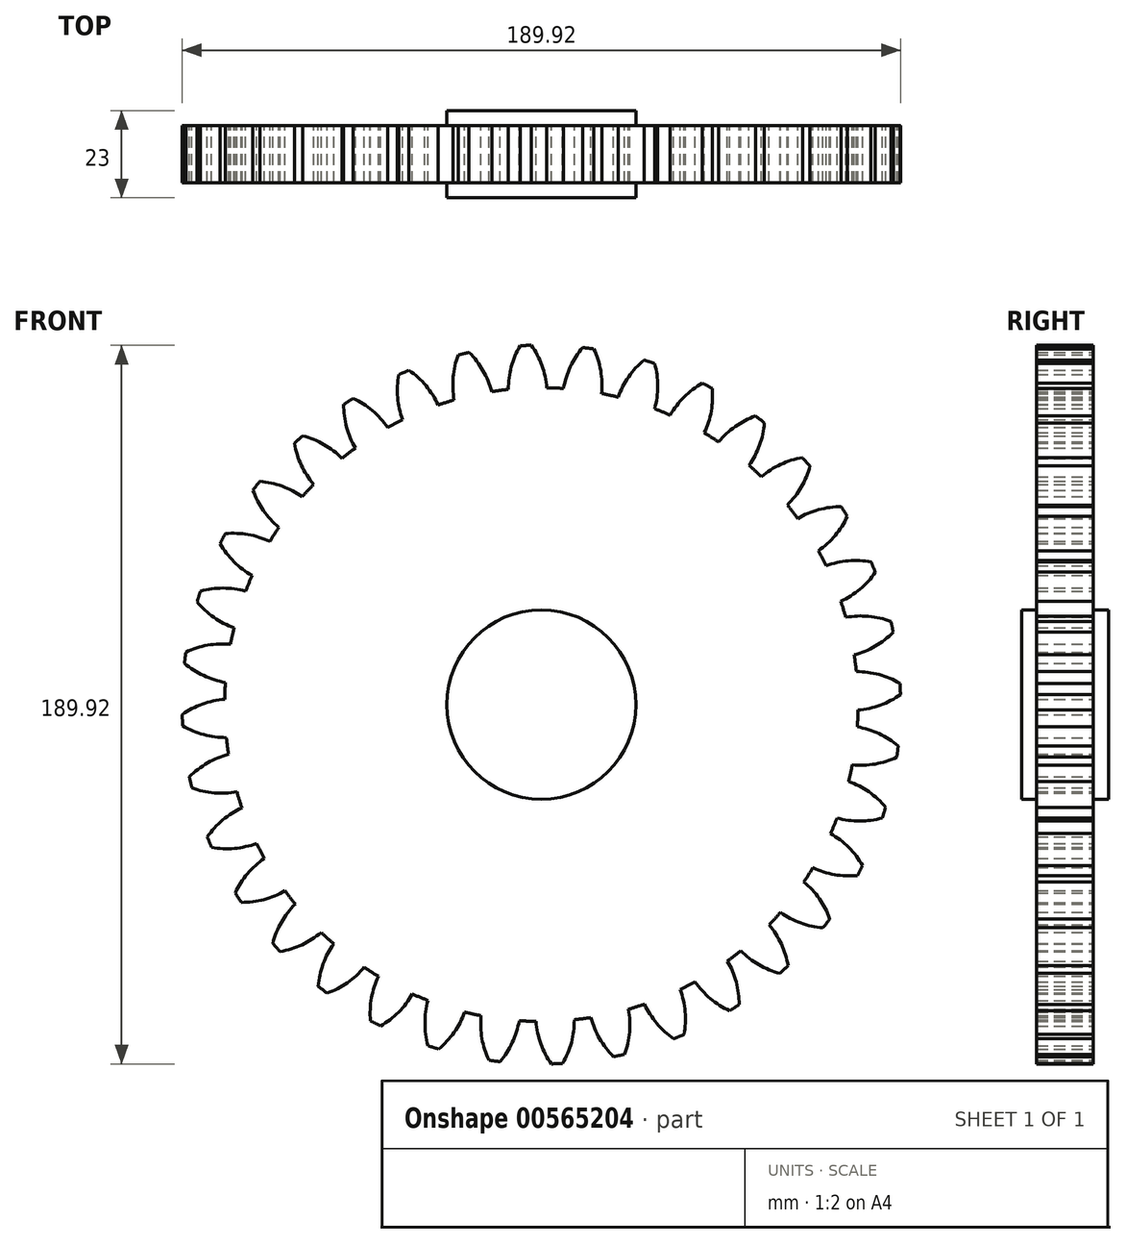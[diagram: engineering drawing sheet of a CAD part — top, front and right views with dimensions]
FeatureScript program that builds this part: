
annotation { "Feature Type Name" : "Feature", "Feature Type Description" : "" }
export const myFeature = defineFeature(function(context is Context, id is Id, definition is map)
    precondition{}
    {
        {
            var Q0;
            Q0=qCreatedBy(makeId("Front.planeOp"),FACE);
            var sketch = newSketch(context, id + "F0", { "sketchPlane" : qUnion([Q0])});
            skCircle(sketch, "E0", {"center": v(0, 0) * mm, "radius": 83.75 * mm});
            skCircle(sketch, "E1", {"center": v(0, 0) * mm, "radius": 90 * mm, "construction": true});
            skCircle(sketch, "E2", {"center": v(0, 0) * mm, "radius": 95 * mm, "construction": true});
            skLineSegment(sketch, "E3", {"start": v(0, 0) * mm, "end": v(0, 175.5) * mm, "construction": true});
            skLineSegment(sketch, "E4", {"start": v(0, 0) * mm, "end": v(-7.83, 179.33) * mm, "construction": true});
            skLineSegment(sketch, "E5", {"start": v(0, 90) * mm, "end": v(-217.65, 90) * mm, "construction": true});
            skLineSegment(sketch, "E6", {"start": v(0, 90) * mm, "end": v(-200.71, 16.95) * mm, "construction": true});
            skCircle(sketch, "E7", {"center": v(0, 0) * mm, "radius": 84.57 * mm, "construction": true});
            skCircle(sketch, "E8", {"center": v(0, 90) * mm, "radius": 22.5 * mm, "construction": true});
            skArc(sketch, "E9", {"start": v(0, 90) * mm, "mid": v(-1.18, 92.57) * mm, "end": v(-2.66, 94.96) * mm});
            skArc(sketch, "E10", {"start": v(1.43, 83.74) * mm, "mid": v(0.94, 86.92) * mm, "end": v(0, 90) * mm});
            skArc(sketch, "E11.MirrorCS", {"start": v(-8.72, 83.3) * mm, "mid": v(-8.5, 86.5) * mm, "end": v(-7.84, 89.66) * mm});
            skArc(sketch, "E12.MirrorCS", {"start": v(-7.84, 89.66) * mm, "mid": v(-6.9, 92.32) * mm, "end": v(-5.62, 94.83) * mm});
            skArc(sketch, "E13", {"start": v(-5.62, 94.83) * mm, "mid": v(-4.14, 94.9) * mm, "end": v(-2.66, 94.96) * mm});
            skCircle(sketch, "E14", {"center": v(0, 0) * mm, "radius": 25 * mm});
            skSolve(sketch);
        }
        {
            var Q0;
            Q0=makeQuery(id+"F0.imprint","IMPRINT",FACE,{"disambiguationData":[TD([[makeQuery(id+"F0.imprint","IMPRINT",EDGE,{"derivedFrom":sQuery(id+"F0.wireOp",EDGE,"E9")}),1.0]])]});
            var Q1;
            {var subQ0=sQuery(id+"F0.wireOp",EDGE,"E0");var subQ1=makeQuery(id+"F0.imprint","INTERSECT",VERTEX,{"derivedFrom":[subQ0,sQuery(id+"F0.wireOp",EDGE,"E10")]});Q1=makeQuery(id+"F0.imprint","IMPRINT",FACE,{"disambiguationData":[TD([[makeQuery(id+"F0.imprint","IMPRINT",EDGE,{"disambiguationData":[TD([[subQ1,-1.0]])],"derivedFrom":subQ0}),1.0]])]});}
            var Q2;
            Q2=makeQuery(id+"F0.imprint","IMPRINT",FACE,{"disambiguationData":[TD([[makeQuery(id+"F0.imprint","IMPRINT",EDGE,{"derivedFrom":sQuery(id+"F0.wireOp",EDGE,"E14")}),1.0]])]});
            extrude(context, id + "F1", {"entities" : qUnion([Q0, Q1, Q2]), "depth" : 15 * mm, "offsetDistance" : 25.4 * mm});
        }
        {
            var Q0;
            Q0=makeQuery(id+"F1.opExtrude","SWEPT_BODY",BODY,{"disambiguationData":[OSD([sQuery(id+"F0.wireOp",EDGE,"E0"),sQuery(id+"F0.wireOp",EDGE,"E9"),sQuery(id+"F0.wireOp",EDGE,"E10"),sQuery(id+"F0.wireOp",EDGE,"E11.MirrorCS"),sQuery(id+"F0.wireOp",EDGE,"E12.MirrorCS"),sQuery(id+"F0.wireOp",EDGE,"E13")])]});
            var Q1;
            Q1=makeQuery(id+"F1.opExtrude","SWEPT_FACE",FACE,{"disambiguationData":[OSD([sQuery(id+"F0.wireOp",EDGE,"E0")])]});
            circularPattern(context, id + "F2", {"entities" : qUnion([Q0]), "axis" : qUnion([Q1]), "angle" : 360 * degree, "instanceCount" : 36, "equalSpace" : true});
        }
        {
            var Q0;
            Q0=makeQuery(id+"F0.imprint","IMPRINT",FACE,{"disambiguationData":[TD([[makeQuery(id+"F0.imprint","IMPRINT",EDGE,{"derivedFrom":sQuery(id+"F0.wireOp",EDGE,"E14")}),1.0]])]});
            extrude(context, id + "F3", {"entities" : qUnion([Q0]), "operationType" : NewBodyOperationType.ADD, "oppositeDirection" : true, "depth" : 4 * mm, "offsetDistance" : 25.4 * mm});
        }
        {
            var Q0;
            Q0=makeQuery(id+"F3.opExtrude","CAP_FACE",FACE,{"disambiguationData":[OSD([sQuery(id+"F0.wireOp",EDGE,"E14")])],"isStart":false});
            extrude(context, id + "F4", {"entities" : qUnion([Q0]), "operationType" : NewBodyOperationType.ADD, "oppositeDirection" : true, "depth" : 23 * mm, "offsetDistance" : 25.4 * mm});
        }
    });
